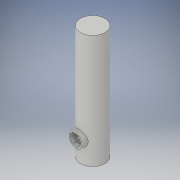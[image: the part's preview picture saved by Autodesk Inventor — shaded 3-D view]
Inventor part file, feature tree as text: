
AUTODESK INVENTOR PART (.ipt)
format: ipt  version: 2017 (Build 210142000, 142)  size: 1,469,952 bytes
history: native  units: in
note: dims shown in document units (in); Inventor stores cm internally (conversion verified against a paired STEP export)
features: extrude x30, sketch x24, other x17, loft x6, shell x1, plane x1, delete_face x1
ambient origin geometry x8: Origin, YZ Plane, XZ Plane, XY Plane, X Axis, Y Axis, Z Axis, Center Point
bodies: Solid6 (feature_tree), Solid7 (feature_tree), Solid8 (feature_tree), Solid9 (feature_tree), Solid10 (feature_tree)
feature tree (80):
  shell  "shell and ramp"  Thickness=15.0in
  extrude  "outer cassing"  Depth=72.0in TaperAngle=0.0deg
  extrude  "bottom"  Depth=1.0in
  sketch  "Sketch2"  dims[d40=1.0in d41=0.0in d44=3.5in]
  other  "Work Axis1"
  other  "ramp"
  other  "ramp light"
  other  "top floor fill workplane"
  extrude  "top floor fill"  Depth=0.5in
  sketch  "Sketch5"  dims[d55=3.0in]
  other  "railing complete"
  other  "light ramp to complete"
  extrude  "top cap"  Depth=1.0in
  plane  "workplane sketch"
  other  "connection plane 1"
  other  "connection plane 2"
  other  "connection workplane 3"
  sketch  "Sketch19"  dims[d64=8.0in d65=1.0in d66=3.1201in d67=0.0in d68=90.0deg d69=90.0deg d70=0.0in d71=0.0in d146=9.0in]
  extrude  "bottom connection"  TaperAngle=90.0deg  [1 undecoded]
  extrude  "bottom connect to case"  TaperAngle=90.0deg  [1 undecoded]
  extrude  "connection cut"  Depth=1.0in TaperAngle=0.0deg
  sketch  "Sketch20"  dims[d147=1.1811in d149=360.0deg d151=90.0deg]
  extrude  "connetion 2"  Depth=9.48in
  extrude  "connection to case 2"  Depth=1.0in TaperAngle=0.0deg
  extrude  "connection cut 2"  Depth=1.0in TaperAngle=0.0deg
  loft  "connection ramp 2"
  sketch  "Sketch22"  dims[d152=90.0deg d153=90.0deg]
  extrude  "connection 3"  Depth=1.0in TaperAngle=0.0deg
  extrude  "connection to case 3"  Depth=1.0in
  extrude  "connection cut 3"  Depth=1.0in TaperAngle=0.0deg
  extrude  "light 3"  Depth=1.0in
  loft  "connetion ramp 3"
  sketch  "Sketch23"  dims[d154=6.6667in d157=4.8944in d158=1.0in d159=0.0in d160=1.0in d161=0.0in]
  extrude  "connection 4"  Depth=4.0in
  extrude  "connection to case 4"  Depth=1.0in TaperAngle=0.0deg
  extrude  "connection cut 4"  TaperAngle=0.0deg  [1 undecoded]
  extrude  "light 4"  Depth=1.0in TaperAngle=0.0deg
  loft  "connection ramp 4"
  sketch  "Sketch24"  dims[d162=2.6875in d163=0.0in d164=9.48in]
  extrude  "connection 5"  Depth=2.0in
  extrude  "connection to case 5"  TaperAngle=90.0deg  [1 undecoded]
  extrude  "connection cut 5"  TaperAngle=90.0deg  [1 undecoded]
  extrude  "light 5"  TaperAngle=0.0deg  [1 undecoded]
  loft  "connection ramp 5"
  sketch  "Sketch25"  dims[d165=6.6667in d168=4.8944in d169=1.0in d170=0.0in d171=1.0in d172=0.0in]
  extrude  "connection 6"  Depth=1.0in
  extrude  "connection to case 6"  Depth=1.0in
  extrude  "connection cut 6"  TaperAngle=0.0deg  [1 undecoded]
  extrude  "light 6"  TaperAngle=0.0deg  [1 undecoded]
  loft  "connection ramp 6"
  sketch  "Sketch26"  dims[d173=2.625in d174=0.0in]
  extrude  "connection 7"  TaperAngle=0.0deg  [1 undecoded]
  extrude  "connection to case 7"  TaperAngle=0.0deg  [1 undecoded]
  extrude  "connection cut 7"  Depth=1.0in
  extrude  "light 7"  TaperAngle=0.0deg  [1 undecoded]
  loft  "connection ramp 7"
  delete_face  "Delete Face1"
  sketch  "Sketch1"  dims[d1=16.0in d2=72.0in d3=0.0in]
  sketch  "Sketch4"  dims[d53=3.0in d54=0.5in]
  sketch  "Sketch27"  dims[d178=6.6667in d179=4.0in d180=1.0in d181=4.8944in d182=1.0in d183=0.0in d184=1.0in d185=0.0in]
  sketch  "Sketch28"  dims[d186=1.0in d187=0.0in d188=20.15in]
  other  "light railing"
  other  "light railing complete"
  sketch  "Sketch29"  dims[d189=30.81in]
  other  "Edges1"
  sketch  "Sketch30"  dims[d190=6.6667in d191=4.0in d192=1.0in d193=4.8944in d194=1.0in d195=0.0in d196=1.0in d197=0.0in]
  other  "Edges2"
  sketch  "Sketch31"  dims[d198=1.0in d199=0.0in d200=41.48in]
  other  "Edges3"
  sketch  "Sketch32"  dims[d201=6.6667in d202=4.0in d203=1.0in d204=4.8944in d205=1.0in d206=0.0in d207=1.0in d208=0.0in]
  other  "Edges4"
  sketch  "Sketch33"  dims[d209=1.0in d210=0.0in d211=52.15in]
  other  "Edges5"
  sketch  "Sketch35"  dims[d213=6.6667in d214=4.0in d215=1.0in d216=4.8944in d217=1.0in d218=0.0in d219=1.0in d220=0.0in]
  other  "Edges6"
  sketch  "Sketch38"  dims[d221=1.0in d222=0.0in d228=6.6667in d229=4.0in d230=1.0in d231=4.8944in]
  sketch  "Sketch39"  dims[d232=62.8in d233=1.0in d234=0.0in]
  sketch  "Sketch40"  dims[d237=1.0in d238=0.0in d239=0.0in]
  sketch  "Sketch41"  dims[d240=1.0in d241=0.0in d242=1.0in d243=0.0in]
  sketch  "Sketch42"  dims[d244=1.0in d245=0.0in d253=0.5833in d254=0.0625in d255=0.0625in d256=0.125in d257=2.0in d268=0.25in d269=0.125in d270=45.0deg d271=0.0892in d272=0.0884in d273=8.0in d274=1.0in d275=3.1201in d276=0.0in d277=90.0deg d278=90.0deg d279=0.0in d280=0.0in d308=3.0in d309=0.5in d310=3.0in d311=0.5833in d312=0.0625in d313=0.0625in d315=0.25in d316=0.125in d317=45.0deg d318=0.0892in d319=0.0884in d320=0.125in d321=90.0deg d322=90.0deg d323=0.0in d324=90.0deg d325=0.0in d326=90.0deg d327=1.0in d329=1.0in d330=0.0in d331=90.0deg d332=0.0in d333=90.0deg d335=1.0in d336=0.0in d337=90.0deg d338=0.0in d339=90.0deg d340=1.0in d341=0.0in d342=90.0deg d343=0.0in d344=90.0deg d346=1.0in d347=0.0in d348=90.0deg d349=0.0in d350=90.0deg d353=1.0in d354=0.0in d355=90.0deg d356=0.0in d357=90.0deg d392=0.5833in d393=0.0625in d394=0.0625in d395=0.125in d396=0.25in d397=0.125in d398=45.0deg d399=0.0892in d400=0.0884in d401=1.0in d402=0.0in d403=0.5833in d404=0.0625in d405=0.0625in d406=0.125in d407=0.25in d408=0.125in d409=45.0deg d410=0.0892in d411=0.0884in d412=1.0in d413=0.0in d414=0.5833in d415=0.0625in d416=0.0625in d417=0.125in d418=0.25in d419=0.125in d420=45.0deg d421=0.0892in d422=0.0884in d423=1.0in d424=0.0in d425=0.5833in d426=0.0625in d427=0.0625in d428=0.125in d429=0.25in d430=0.125in d431=45.0deg d432=0.0892in d433=0.0884in d434=1.0in d435=0.0in d436=0.25in d437=0.125in d438=45.0deg d439=0.0892in d440=0.0884in d441=0.5833in d442=0.0625in d443=0.0625in d444=0.125in d445=1.0in d446=0.0in d448=4.0in d449=0.5833in d450=3.8873in d451=3.8873in d452=1.7083in d453=0.0625in d454=0.0625in d455=1.6458in d456=0.25in d457=0.125in d458=0.0884in d459=45.0deg d460=3.3333in d461=0.125in d462=1.0in d463=4.0in d464=0.5833in d465=3.8873in d466=3.8873in d467=1.7083in d468=0.0625in d469=0.0625in d470=1.6458in d471=0.25in d472=0.125in d473=0.0884in d474=45.0deg d475=3.3333in d476=0.125in d477=1.0in]
note: 11 required parameter values undecoded (feature->parameter linkage not recoverable at this tier; creation-order binding heuristic only, values carry confidence <= 0.55)
